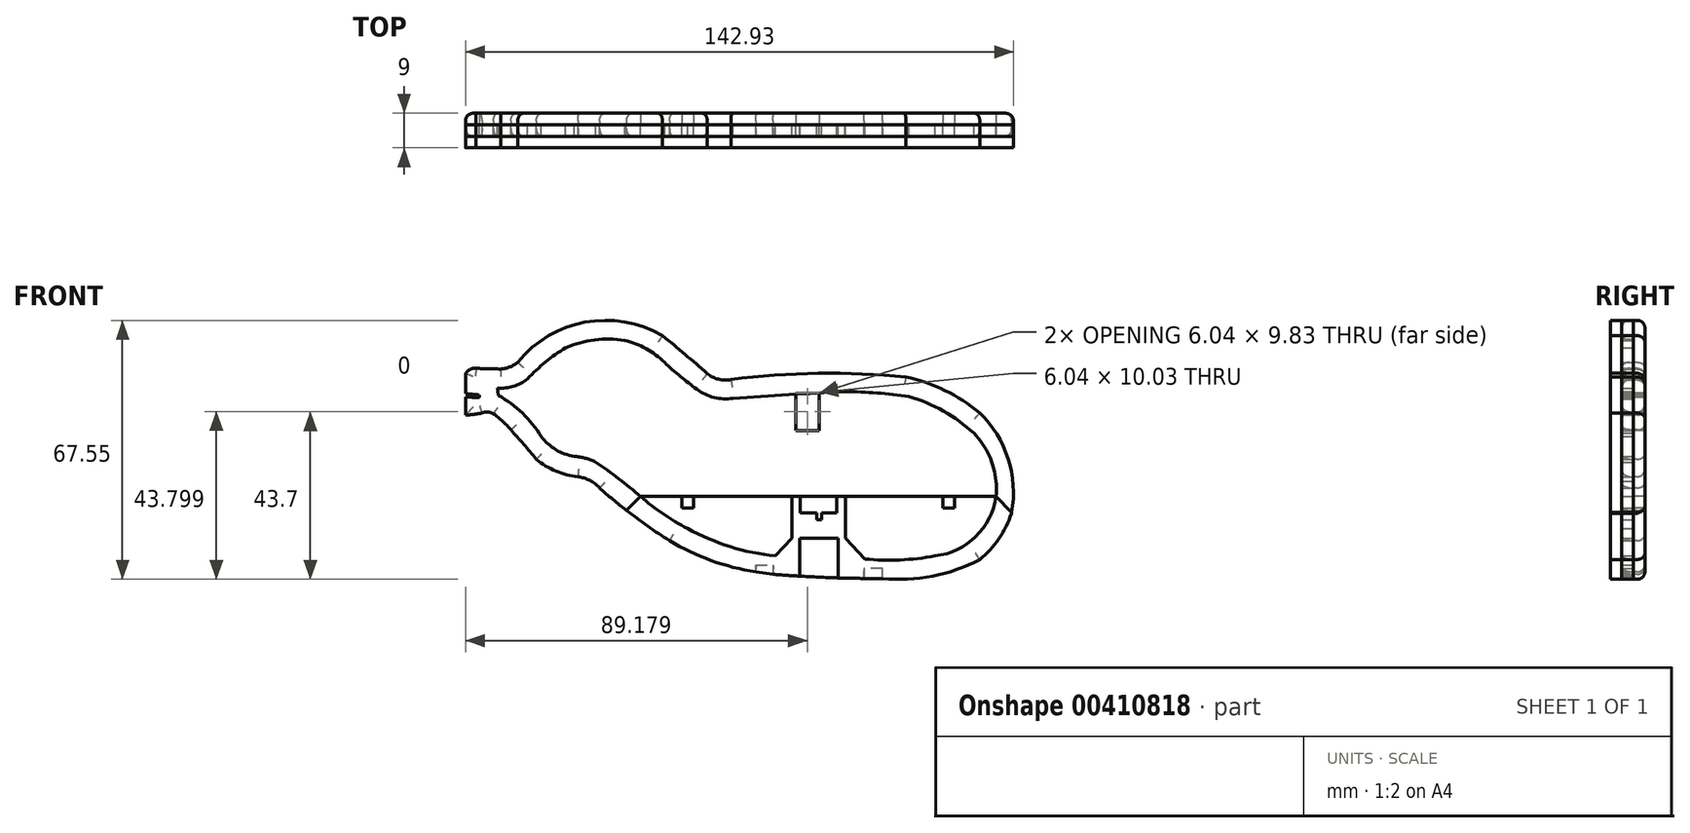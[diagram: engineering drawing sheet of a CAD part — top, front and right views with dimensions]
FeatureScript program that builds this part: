
annotation { "Feature Type Name" : "Feature", "Feature Type Description" : "" }
export const myFeature = defineFeature(function(context is Context, id is Id, definition is map)
    precondition{}
    {
        {
            var Q0;
            Q0=qCreatedBy(makeId("Front.planeOp"),FACE);
            var sketch = newSketch(context, id + "F0", { "sketchPlane" : qUnion([Q0])});
            skArc(sketch, "E0", {"start": v(-22.58, 34.57) * mm, "mid": v(-42.73, 38.11) * mm, "end": v(-60.32, 27.66) * mm});
            skArc(sketch, "E1", {"start": v(-10.89, 24.63) * mm, "mid": v(-16.66, 29.68) * mm, "end": v(-22.58, 34.57) * mm});
            skArc(sketch, "E2", {"start": v(-10.89, 24.63) * mm, "mid": v(-7.95, 23.24) * mm, "end": v(-4.7, 23.15) * mm});
            skArc(sketch, "E3", {"start": v(40.9, 23.83) * mm, "mid": v(18.08, 24.76) * mm, "end": v(-4.7, 23.15) * mm});
            skArc(sketch, "E4", {"start": v(60.17, 14.42) * mm, "mid": v(51.11, 20.3) * mm, "end": v(40.9, 23.83) * mm});
            skArc(sketch, "E5", {"start": v(68.44, -11.76) * mm, "mid": v(67.63, 2.38) * mm, "end": v(60.17, 14.42) * mm});
            skArc(sketch, "E6", {"start": v(60.17, -23.8) * mm, "mid": v(65.16, -18.37) * mm, "end": v(68.44, -11.76) * mm});
            skArc(sketch, "E7", {"start": v(34.76, -28.73) * mm, "mid": v(47.83, -28.14) * mm, "end": v(60.17, -23.8) * mm});
            skArc(sketch, "E8", {"start": v(-20.75, -18.88) * mm, "mid": v(-9.89, -24.03) * mm, "end": v(1.76, -27.02) * mm});
            skArc(sketch, "E9", {"start": v(-39, -5.12) * mm, "mid": v(-30.15, -12.37) * mm, "end": v(-20.75, -18.88) * mm});
            skArc(sketch, "E10", {"start": v(-39, -5.12) * mm, "mid": v(-41.52, -3.16) * mm, "end": v(-44.58, -2.2) * mm});
            skArc(sketch, "E11", {"start": v(-55.48, 2.36) * mm, "mid": v(-50.37, -0.73) * mm, "end": v(-44.58, -2.2) * mm});
            skArc(sketch, "E12", {"start": v(-55.48, 2.36) * mm, "mid": v(-58.75, 6.24) * mm, "end": v(-62.14, 10.03) * mm});
            skArc(sketch, "E13", {"start": v(-62.14, 10.03) * mm, "mid": v(-64.26, 12.25) * mm, "end": v(-66.65, 14.2) * mm});
            skArc(sketch, "E14", {"start": v(-66.65, 14.2) * mm, "mid": v(-68.1, 14.69) * mm, "end": v(-69.6, 14.44) * mm});
            skArc(sketch, "E15", {"start": v(-73.93, 13.86) * mm, "mid": v(-71.75, 14.07) * mm, "end": v(-69.6, 14.44) * mm});
            skArc(sketch, "E16", {"start": v(-73.93, 18.66) * mm, "mid": v(-73.95, 16.26) * mm, "end": v(-73.93, 13.86) * mm});
            skArc(sketch, "E17", {"start": v(-73.93, 18.66) * mm, "mid": v(-72.16, 18.52) * mm, "end": v(-70.38, 18.41) * mm});
            skArc(sketch, "E18", {"start": v(-70.38, 18.41) * mm, "mid": v(-70.33, 18.77) * mm, "end": v(-70.38, 19.13) * mm});
            skArc(sketch, "E19", {"start": v(-70.38, 19.13) * mm, "mid": v(-72.15, 19.31) * mm, "end": v(-73.93, 19.46) * mm});
            skArc(sketch, "E20", {"start": v(-73.93, 24.73) * mm, "mid": v(-73.96, 22.1) * mm, "end": v(-73.93, 19.46) * mm});
            skArc(sketch, "E21", {"start": v(-71.2, 26.08) * mm, "mid": v(-72.76, 25.8) * mm, "end": v(-73.93, 24.73) * mm});
            skArc(sketch, "E22", {"start": v(-71.2, 26.08) * mm, "mid": v(-68, 25.93) * mm, "end": v(-64.8, 25.9) * mm});
            skArc(sketch, "E23", {"start": v(-64.8, 25.9) * mm, "mid": v(-62.41, 26.4) * mm, "end": v(-60.32, 27.66) * mm});
            skLineSegment(sketch, "E24", {"start": v(1.76, -27.02) * mm, "end": v(1.76, -25.28) * mm});
            skLineSegment(sketch, "E25", {"start": v(1.76, -25.28) * mm, "end": v(6.25, -25.28) * mm});
            skLineSegment(sketch, "E26", {"start": v(6.25, -25.28) * mm, "end": v(6.25, -27.65) * mm});
            skLineSegment(sketch, "E27", {"start": v(34.76, -28.73) * mm, "end": v(34.76, -26.12) * mm});
            skLineSegment(sketch, "E28", {"start": v(34.76, -26.12) * mm, "end": v(30.01, -26.12) * mm});
            skLineSegment(sketch, "E29", {"start": v(30.01, -26.12) * mm, "end": v(30.01, -28.73) * mm});
            skArc(sketch, "E30", {"start": v(6.25, -27.65) * mm, "mid": v(18.13, -28.4) * mm, "end": v(30.01, -28.73) * mm});
            skLineSegment(sketch, "E31", {"start": v(-31.93, -11) * mm, "end": v(-28.25, -7.37) * mm});
            skLineSegment(sketch, "E32", {"start": v(68.52, -11.52) * mm, "end": v(64.41, -7.34) * mm});
            skLineSegment(sketch, "E33", {"start": v(-28.25, -7.37) * mm, "end": v(64.41, -7.34) * mm});
            skArc(sketch, "E34", {"start": v(-65.6, 20.9) * mm, "mid": v(-61.47, 21.4) * mm, "end": v(-57.78, 23.3) * mm});
            skArc(sketch, "E35", {"start": v(-47.8, 31.46) * mm, "mid": v(-53.07, 27.71) * mm, "end": v(-57.78, 23.3) * mm});
            skArc(sketch, "E36", {"start": v(-32.42, 33.36) * mm, "mid": v(-40.25, 33.5) * mm, "end": v(-47.8, 31.46) * mm});
            skArc(sketch, "E37", {"start": v(-22.02, 27.61) * mm, "mid": v(-26.83, 31.2) * mm, "end": v(-32.42, 33.36) * mm});
            skArc(sketch, "E38", {"start": v(-22.02, 27.61) * mm, "mid": v(-17.93, 23.98) * mm, "end": v(-13.61, 20.6) * mm});
            skArc(sketch, "E39", {"start": v(-13.61, 20.6) * mm, "mid": v(-9.14, 18.48) * mm, "end": v(-4.19, 18.23) * mm});
            skArc(sketch, "E40", {"start": v(25, 19.97) * mm, "mid": v(10.4, 19.22) * mm, "end": v(-4.19, 18.23) * mm});
            skArc(sketch, "E41", {"start": v(41.7, 18.7) * mm, "mid": v(33.37, 19.66) * mm, "end": v(25, 19.97) * mm});
            skArc(sketch, "E42", {"start": v(58.64, 9.15) * mm, "mid": v(50.71, 14.9) * mm, "end": v(41.7, 18.7) * mm});
            skArc(sketch, "E43", {"start": v(64.41, -3.4) * mm, "mid": v(62.63, 3.38) * mm, "end": v(58.64, 9.15) * mm});
            skArc(sketch, "E44", {"start": v(64.41, -7.34) * mm, "mid": v(64.58, -5.38) * mm, "end": v(64.41, -3.4) * mm});
            skArc(sketch, "E45", {"start": v(48.53, -22.85) * mm, "mid": v(59.13, -17.82) * mm, "end": v(64.41, -7.34) * mm});
            skArc(sketch, "E46", {"start": v(30.22, -23.66) * mm, "mid": v(39.4, -23.89) * mm, "end": v(48.53, -22.85) * mm});
            skArc(sketch, "E47", {"start": v(-16, -15.7) * mm, "mid": v(-4.93, -20.45) * mm, "end": v(6.88, -22.85) * mm});
            skArc(sketch, "E48", {"start": v(-28.25, -7.37) * mm, "mid": v(-22.4, -11.93) * mm, "end": v(-16, -15.7) * mm});
            skArc(sketch, "E49", {"start": v(-28.25, -7.37) * mm, "mid": v(-33.99, -2.7) * mm, "end": v(-40, 1.63) * mm});
            skArc(sketch, "E50", {"start": v(-40, 1.63) * mm, "mid": v(-42.75, 2.66) * mm, "end": v(-45.64, 3.14) * mm});
            skArc(sketch, "E51", {"start": v(-54.18, 8.27) * mm, "mid": v(-50.42, 4.86) * mm, "end": v(-45.64, 3.14) * mm});
            skArc(sketch, "E52", {"start": v(-54.18, 8.27) * mm, "mid": v(-59.1, 14.36) * mm, "end": v(-65.38, 19.04) * mm});
            skArc(sketch, "E53", {"start": v(-65.6, 20.9) * mm, "mid": v(-65.5, 19.96) * mm, "end": v(-65.38, 19.04) * mm});
            skLineSegment(sketch, "E54", {"start": v(13.17, -28.13) * mm, "end": v(13.17, -18.3) * mm});
            skLineSegment(sketch, "E55", {"start": v(13.17, -18.3) * mm, "end": v(23.23, -18.3) * mm});
            skLineSegment(sketch, "E56", {"start": v(23.23, -18.3) * mm, "end": v(23.23, -28.59) * mm});
            skLineSegment(sketch, "E57", {"start": v(6.88, -22.85) * mm, "end": v(11.22, -18.3) * mm});
            skLineSegment(sketch, "E58", {"start": v(11.22, -18.3) * mm, "end": v(11.22, -7.36) * mm});
            skLineSegment(sketch, "E59", {"start": v(13.33, -7.36) * mm, "end": v(13.33, -11.63) * mm});
            skLineSegment(sketch, "E60", {"start": v(13.33, -11.63) * mm, "end": v(17.72, -11.63) * mm});
            skLineSegment(sketch, "E61", {"start": v(17.72, -11.63) * mm, "end": v(17.72, -13.39) * mm});
            skLineSegment(sketch, "E62", {"start": v(17.72, -13.39) * mm, "end": v(18.88, -13.39) * mm});
            skLineSegment(sketch, "E63", {"start": v(18.88, -13.39) * mm, "end": v(18.88, -11.63) * mm});
            skLineSegment(sketch, "E64", {"start": v(18.88, -11.63) * mm, "end": v(22.87, -11.63) * mm});
            skLineSegment(sketch, "E65", {"start": v(22.87, -11.63) * mm, "end": v(22.86, -7.35) * mm});
            skLineSegment(sketch, "E66", {"start": v(25.1, -7.35) * mm, "end": v(25.1, -18.3) * mm});
            skLineSegment(sketch, "E67", {"start": v(25.1, -18.3) * mm, "end": v(30.22, -23.66) * mm});
            skLineSegment(sketch, "E68", {"start": v(-17.45, -7.36) * mm, "end": v(-17.45, -10.4) * mm});
            skLineSegment(sketch, "E69", {"start": v(-17.45, -10.4) * mm, "end": v(-14.45, -10.4) * mm});
            skLineSegment(sketch, "E70", {"start": v(-14.45, -10.4) * mm, "end": v(-14.45, -7.36) * mm});
            skLineSegment(sketch, "E71", {"start": v(50.57, -7.35) * mm, "end": v(50.57, -10.4) * mm});
            skLineSegment(sketch, "E72", {"start": v(50.57, -10.4) * mm, "end": v(53.57, -10.4) * mm});
            skLineSegment(sketch, "E73", {"start": v(53.57, -10.4) * mm, "end": v(53.57, -7.35) * mm});
            skLineSegment(sketch, "E74.bottom", {"start": v(12.2, 19.85) * mm, "end": v(18.24, 19.85) * mm});
            skLineSegment(sketch, "E74.top", {"start": v(12.2, 9.82) * mm, "end": v(18.24, 9.82) * mm});
            skLineSegment(sketch, "E74.left", {"start": v(12.2, 19.85) * mm, "end": v(12.2, 9.82) * mm});
            skLineSegment(sketch, "E74.right", {"start": v(18.24, 19.85) * mm, "end": v(18.24, 9.82) * mm});
            skLineSegment(sketch, "E75", {"start": v(1.76, -27.02) * mm, "end": v(6.25, -27.65) * mm});
            skLineSegment(sketch, "E76", {"start": v(30.01, -28.73) * mm, "end": v(34.76, -28.73) * mm});
            skLineSegment(sketch, "E77.bottom", {"start": v(11.2, -7.36) * mm, "end": v(-3.8, -7.36) * mm});
            skLineSegment(sketch, "E77.top", {"start": v(8.2, 6.4) * mm, "end": v(-0.8, 6.4) * mm});
            skLineSegment(sketch, "E77.left", {"start": v(11.2, -7.36) * mm, "end": v(11.2, 3.4) * mm});
            skLineSegment(sketch, "E77.right", {"start": v(-3.8, -7.36) * mm, "end": v(-3.8, 3.4) * mm});
            skLineSegment(sketch, "E78.bottom", {"start": v(28.16, 6.4) * mm, "end": v(37.16, 6.4) * mm});
            skLineSegment(sketch, "E78.top", {"start": v(25.16, -7.35) * mm, "end": v(40.16, -7.35) * mm});
            skLineSegment(sketch, "E78.left", {"start": v(25.16, 3.4) * mm, "end": v(25.16, -7.35) * mm});
            skLineSegment(sketch, "E78.right", {"start": v(40.16, 3.4) * mm, "end": v(40.16, -7.35) * mm});
            skLineSegment(sketch, "E79", {"start": v(-35.06, -1.89) * mm, "end": v(64.23, -1.89) * mm});
            skPoint(sketch, "E80.visualSharp", {"position": v(11.2, 6.4) * mm});
            skArc(sketch, "E80.filletArc", {"start": v(11.2, 3.4) * mm, "mid": v(10.32, 5.52) * mm, "end": v(8.2, 6.4) * mm});
            skPoint(sketch, "E81.visualSharp", {"position": v(-3.8, 6.4) * mm});
            skArc(sketch, "E81.filletArc", {"start": v(-0.8, 6.4) * mm, "mid": v(-2.92, 5.52) * mm, "end": v(-3.8, 3.4) * mm});
            skPoint(sketch, "E82.visualSharp", {"position": v(25.16, 6.4) * mm});
            skArc(sketch, "E82.filletArc", {"start": v(28.16, 6.4) * mm, "mid": v(26.04, 5.52) * mm, "end": v(25.16, 3.4) * mm});
            skPoint(sketch, "E83.visualSharp", {"position": v(40.16, 6.4) * mm});
            skArc(sketch, "E83.filletArc", {"start": v(40.16, 3.4) * mm, "mid": v(39.28, 5.52) * mm, "end": v(37.16, 6.4) * mm});
            skSolve(sketch);
        }
        {
            var Q0;
            Q0 = qSketchRegion(id + "F0", true);
            var Q1;
            Q1=makeQuery(id+"F0.imprint","IMPRINT",FACE,{"disambiguationData":[TD([[makeQuery(id+"F0.imprint","IMPRINT",EDGE,{"derivedFrom":sQuery(id+"F0.wireOp",EDGE,"E34")}),-1.0]])]});
            var Q2;
            Q2=makeQuery(id+"F0.imprint","IMPRINT",FACE,{"disambiguationData":[TD([[makeQuery(id+"F0.imprint","IMPRINT",EDGE,{"derivedFrom":sQuery(id+"F0.wireOp",EDGE,"E47")}),1.0]])]});
            var Q3;
            {var subQ0=sQuery(id+"F0.wireOp",EDGE,"E45");Q3=makeQuery(id+"F0.imprint","IMPRINT",FACE,{"disambiguationData":[TD([[makeQuery(id+"F0.imprint","IMPRINT",EDGE,{"derivedFrom":subQ0}),1.0]])]});}
            var Q4;
            Q4=makeQuery(id+"F0.imprint","IMPRINT",FACE,{"disambiguationData":[TD([[makeQuery(id+"F0.imprint","IMPRINT",EDGE,{"derivedFrom":sQuery(id+"F0.wireOp",EDGE,"E78.bottom")}),-1.0]])]});
            var Q5;
            Q5=makeQuery(id+"F0.imprint","IMPRINT",FACE,{"disambiguationData":[TD([[makeQuery(id+"F0.imprint","IMPRINT",EDGE,{"derivedFrom":sQuery(id+"F0.wireOp",EDGE,"E77.top")}),1.0]])]});
            var Q6;
            {var subQ0=sQuery(id+"F0.wireOp",EDGE,"E59");Q6=makeQuery(id+"F0.imprint","IMPRINT",FACE,{"disambiguationData":[TD([[makeQuery(id+"F0.imprint","IMPRINT",EDGE,{"derivedFrom":subQ0}),1.0]])]});}
            var Q7;
            {var subQ4=sQuery(id+"F0.wireOp",EDGE,"E78.top");Q7=makeQuery(id+"F0.imprint","IMPRINT",FACE,{"disambiguationData":[TD([[makeQuery(id+"F0.imprint","IMPRINT",EDGE,{"derivedFrom":subQ4}),-1.0]])]});}
            var Q8;
            {var subQ0=sQuery(id+"F0.wireOp",EDGE,"E78.top");Q8=makeQuery(id+"F0.imprint","IMPRINT",FACE,{"disambiguationData":[TD([[makeQuery(id+"F0.imprint","IMPRINT",EDGE,{"derivedFrom":subQ0}),1.0]])]});}
            var Q9;
            {var subQ0=sQuery(id+"F0.wireOp",EDGE,"E44");Q9=makeQuery(id+"F0.imprint","IMPRINT",FACE,{"disambiguationData":[TD([[makeQuery(id+"F0.imprint","IMPRINT",EDGE,{"derivedFrom":subQ0}),1.0]])]});}
            var Q10;
            {var subQ0=sQuery(id+"F0.wireOp",EDGE,"E77.bottom");Q10=makeQuery(id+"F0.imprint","IMPRINT",FACE,{"disambiguationData":[TD([[makeQuery(id+"F0.imprint","IMPRINT",EDGE,{"derivedFrom":subQ0}),-1.0]])]});}
            var Q11;
            {var subQ6=sQuery(id+"F0.wireOp",EDGE,"E77.bottom");Q11=makeQuery(id+"F0.imprint","IMPRINT",FACE,{"disambiguationData":[TD([[makeQuery(id+"F0.imprint","IMPRINT",EDGE,{"derivedFrom":subQ6}),1.0]])]});}
            var Q12;
            {var subQ5=sQuery(id+"F0.wireOp",EDGE,"E74.top");Q12=makeQuery(id+"F0.imprint","IMPRINT",FACE,{"disambiguationData":[TD([[makeQuery(id+"F0.imprint","IMPRINT",EDGE,{"derivedFrom":subQ5}),1.0]])]});}
            var Q13;
            {var subQ0=sQuery(id+"F0.wireOp",EDGE,"E71");Q13=makeQuery(id+"F0.imprint","IMPRINT",FACE,{"disambiguationData":[TD([[makeQuery(id+"F0.imprint","IMPRINT",EDGE,{"derivedFrom":subQ0}),1.0]])]});}
            var Q14;
            {var subQ0=sQuery(id+"F0.wireOp",EDGE,"E68");Q14=makeQuery(id+"F0.imprint","IMPRINT",FACE,{"disambiguationData":[TD([[makeQuery(id+"F0.imprint","IMPRINT",EDGE,{"derivedFrom":subQ0}),1.0]])]});}
            var Q15;
            {var subQ5=sQuery(id+"F0.wireOp",EDGE,"E74.bottom");Q15=makeQuery(id+"F0.imprint","IMPRINT",FACE,{"disambiguationData":[TD([[makeQuery(id+"F0.imprint","IMPRINT",EDGE,{"derivedFrom":subQ5}),-1.0]])]});}
            extrude(context, id + "F1", {"entities" : qUnion([Q0, Q1, Q2, Q3, Q4, Q5, Q6, Q7, Q8, Q9, Q10, Q11, Q12, Q13, Q14, Q15]), "depth" : 3 * mm, "offsetDistance" : 25 * mm});
        }
        {
            var Q0;
            Q0=makeQuery(id+"F0.imprint","IMPRINT",FACE,{"disambiguationData":[TD([[makeQuery(id+"F0.imprint","IMPRINT",EDGE,{"derivedFrom":sQuery(id+"F0.wireOp",EDGE,"E0")}),1.0]])]});
            extrude(context, id + "F2", {"entities" : qUnion([Q0]), "depth" : 3 * mm, "offsetDistance" : 25 * mm});
        }
        {
            var Q0;
            Q0=makeQuery(id+"F0.imprint","IMPRINT",FACE,{"disambiguationData":[TD([[makeQuery(id+"F0.imprint","IMPRINT",EDGE,{"derivedFrom":sQuery(id+"F0.wireOp",EDGE,"E34")}),-1.0]])]});
            var Q1;
            Q1=makeQuery(id+"F0.imprint","IMPRINT",FACE,{"disambiguationData":[TD([[makeQuery(id+"F0.imprint","IMPRINT",EDGE,{"derivedFrom":sQuery(id+"F0.wireOp",EDGE,"E77.top")}),1.0]])]});
            var Q2;
            Q2=makeQuery(id+"F0.imprint","IMPRINT",FACE,{"disambiguationData":[TD([[makeQuery(id+"F0.imprint","IMPRINT",EDGE,{"derivedFrom":sQuery(id+"F0.wireOp",EDGE,"E78.bottom")}),-1.0]])]});
            var Q3;
            Q3=makeQuery(id+"F0.imprint","IMPRINT",FACE,{"disambiguationData":[TD([[makeQuery(id+"F0.imprint","IMPRINT",EDGE,{"derivedFrom":sQuery(id+"F0.wireOp",EDGE,"E0")}),1.0]])]});
            var Q4;
            {var subQ6=sQuery(id+"F0.wireOp",EDGE,"E77.bottom");Q4=makeQuery(id+"F0.imprint","IMPRINT",FACE,{"disambiguationData":[TD([[makeQuery(id+"F0.imprint","IMPRINT",EDGE,{"derivedFrom":subQ6}),1.0]])]});}
            var Q5;
            {var subQ0=sQuery(id+"F0.wireOp",EDGE,"E77.bottom");Q5=makeQuery(id+"F0.imprint","IMPRINT",FACE,{"disambiguationData":[TD([[makeQuery(id+"F0.imprint","IMPRINT",EDGE,{"derivedFrom":subQ0}),-1.0]])]});}
            var Q6;
            {var subQ0=sQuery(id+"F0.wireOp",EDGE,"E44");Q6=makeQuery(id+"F0.imprint","IMPRINT",FACE,{"disambiguationData":[TD([[makeQuery(id+"F0.imprint","IMPRINT",EDGE,{"derivedFrom":subQ0}),1.0]])]});}
            var Q7;
            {var subQ0=sQuery(id+"F0.wireOp",EDGE,"E78.top");Q7=makeQuery(id+"F0.imprint","IMPRINT",FACE,{"disambiguationData":[TD([[makeQuery(id+"F0.imprint","IMPRINT",EDGE,{"derivedFrom":subQ0}),1.0]])]});}
            var Q8;
            {var subQ4=sQuery(id+"F0.wireOp",EDGE,"E78.top");Q8=makeQuery(id+"F0.imprint","IMPRINT",FACE,{"disambiguationData":[TD([[makeQuery(id+"F0.imprint","IMPRINT",EDGE,{"derivedFrom":subQ4}),-1.0]])]});}
            extrude(context, id + "F3", {"entities" : qUnion([Q0, Q1, Q2, Q3, Q4, Q5, Q6, Q7, Q8]), "depth" : 3 * mm, "offsetDistance" : 25 * mm});
        }
        {
            var Q0;
            Q0=makeQuery(id+"F1.opExtrude","SWEPT_BODY",BODY,{"disambiguationData":[OSD([sQuery(id+"F0.wireOp",EDGE,"E0"),sQuery(id+"F0.wireOp",EDGE,"E1"),sQuery(id+"F0.wireOp",EDGE,"E2"),sQuery(id+"F0.wireOp",EDGE,"E3"),sQuery(id+"F0.wireOp",EDGE,"E4"),sQuery(id+"F0.wireOp",EDGE,"E5"),sQuery(id+"F0.wireOp",EDGE,"E6"),sQuery(id+"F0.wireOp",EDGE,"E7"),sQuery(id+"F0.wireOp",EDGE,"E8"),sQuery(id+"F0.wireOp",EDGE,"E9"),sQuery(id+"F0.wireOp",EDGE,"E10"),sQuery(id+"F0.wireOp",EDGE,"E11"),sQuery(id+"F0.wireOp",EDGE,"E12"),sQuery(id+"F0.wireOp",EDGE,"E13"),sQuery(id+"F0.wireOp",EDGE,"E14"),sQuery(id+"F0.wireOp",EDGE,"E15"),sQuery(id+"F0.wireOp",EDGE,"E16"),sQuery(id+"F0.wireOp",EDGE,"E17"),sQuery(id+"F0.wireOp",EDGE,"E18"),sQuery(id+"F0.wireOp",EDGE,"E19"),sQuery(id+"F0.wireOp",EDGE,"E20"),sQuery(id+"F0.wireOp",EDGE,"E21"),sQuery(id+"F0.wireOp",EDGE,"E22"),sQuery(id+"F0.wireOp",EDGE,"E23"),sQuery(id+"F0.wireOp",EDGE,"E30"),sQuery(id+"F0.wireOp",EDGE,"E75"),sQuery(id+"F0.wireOp",EDGE,"E76")])]});
            deleteBodies(context, id + "F4", {"entities" : qUnion([Q0])});
        }
        {
            var Q0;
            Q0=makeQuery(id+"F0.imprint","IMPRINT",FACE,{"disambiguationData":[TD([[makeQuery(id+"F0.imprint","IMPRINT",EDGE,{"derivedFrom":sQuery(id+"F0.wireOp",EDGE,"E0")}),1.0]])]});
            var Q1;
            Q1=makeQuery(id+"F0.imprint","IMPRINT",FACE,{"disambiguationData":[TD([[makeQuery(id+"F0.imprint","IMPRINT",EDGE,{"derivedFrom":sQuery(id+"F0.wireOp",EDGE,"E34")}),-1.0]])]});
            var Q2;
            Q2=makeQuery(id+"F0.imprint","IMPRINT",FACE,{"disambiguationData":[TD([[makeQuery(id+"F0.imprint","IMPRINT",EDGE,{"derivedFrom":sQuery(id+"F0.wireOp",EDGE,"E77.top")}),1.0]])]});
            var Q3;
            {var subQ0=sQuery(id+"F0.wireOp",EDGE,"E77.bottom");Q3=makeQuery(id+"F0.imprint","IMPRINT",FACE,{"disambiguationData":[TD([[makeQuery(id+"F0.imprint","IMPRINT",EDGE,{"derivedFrom":subQ0}),-1.0]])]});}
            var Q4;
            {var subQ4=sQuery(id+"F0.wireOp",EDGE,"E78.top");Q4=makeQuery(id+"F0.imprint","IMPRINT",FACE,{"disambiguationData":[TD([[makeQuery(id+"F0.imprint","IMPRINT",EDGE,{"derivedFrom":subQ4}),-1.0]])]});}
            var Q5;
            {var subQ0=sQuery(id+"F0.wireOp",EDGE,"E78.top");Q5=makeQuery(id+"F0.imprint","IMPRINT",FACE,{"disambiguationData":[TD([[makeQuery(id+"F0.imprint","IMPRINT",EDGE,{"derivedFrom":subQ0}),1.0]])]});}
            var Q6;
            Q6=makeQuery(id+"F0.imprint","IMPRINT",FACE,{"disambiguationData":[TD([[makeQuery(id+"F0.imprint","IMPRINT",EDGE,{"derivedFrom":sQuery(id+"F0.wireOp",EDGE,"E78.bottom")}),-1.0]])]});
            var Q7;
            {var subQ0=sQuery(id+"F0.wireOp",EDGE,"E44");Q7=makeQuery(id+"F0.imprint","IMPRINT",FACE,{"disambiguationData":[TD([[makeQuery(id+"F0.imprint","IMPRINT",EDGE,{"derivedFrom":subQ0}),1.0]])]});}
            var Q8;
            {var subQ6=sQuery(id+"F0.wireOp",EDGE,"E77.bottom");Q8=makeQuery(id+"F0.imprint","IMPRINT",FACE,{"disambiguationData":[TD([[makeQuery(id+"F0.imprint","IMPRINT",EDGE,{"derivedFrom":subQ6}),1.0]])]});}
            var Q9;
            {var subQ5=sQuery(id+"F0.wireOp",EDGE,"E74.bottom");Q9=makeQuery(id+"F0.imprint","IMPRINT",FACE,{"disambiguationData":[TD([[makeQuery(id+"F0.imprint","IMPRINT",EDGE,{"derivedFrom":subQ5}),-1.0]])]});}
            extrude(context, id + "F5", {"entities" : qUnion([Q0, Q1, Q2, Q3, Q4, Q5, Q6, Q7, Q8, Q9]), "depth" : 3 * mm, "offsetDistance" : 25 * mm});
        }
        {
            var Q0;
            Q0=makeQuery(id+"F0.imprint","IMPRINT",FACE,{"disambiguationData":[TD([[makeQuery(id+"F0.imprint","IMPRINT",EDGE,{"derivedFrom":sQuery(id+"F0.wireOp",EDGE,"E0")}),1.0]])]});
            var Q1;
            {var subQ5=sQuery(id+"F0.wireOp",EDGE,"E74.bottom");Q1=makeQuery(id+"F0.imprint","IMPRINT",FACE,{"disambiguationData":[TD([[makeQuery(id+"F0.imprint","IMPRINT",EDGE,{"derivedFrom":subQ5}),-1.0]])]});}
            extrude(context, id + "F6", {"entities" : qUnion([Q0, Q1]), "depth" : 6 * mm, "offsetDistance" : 25 * mm});
        }
        {
            var Q0;
            Q0=makeQuery(id+"F0.imprint","IMPRINT",FACE,{"disambiguationData":[TD([[makeQuery(id+"F0.imprint","IMPRINT",EDGE,{"derivedFrom":sQuery(id+"F0.wireOp",EDGE,"E0")}),1.0]])]});
            var Q1;
            Q1=makeQuery(id+"F0.imprint","IMPRINT",FACE,{"disambiguationData":[TD([[makeQuery(id+"F0.imprint","IMPRINT",EDGE,{"derivedFrom":sQuery(id+"F0.wireOp",EDGE,"E34")}),-1.0]])]});
            var Q2;
            {var subQ0=sQuery(id+"F0.wireOp",EDGE,"E77.bottom");Q2=makeQuery(id+"F0.imprint","IMPRINT",FACE,{"disambiguationData":[TD([[makeQuery(id+"F0.imprint","IMPRINT",EDGE,{"derivedFrom":subQ0}),-1.0]])]});}
            var Q3;
            {var subQ0=sQuery(id+"F0.wireOp",EDGE,"E78.top");Q3=makeQuery(id+"F0.imprint","IMPRINT",FACE,{"disambiguationData":[TD([[makeQuery(id+"F0.imprint","IMPRINT",EDGE,{"derivedFrom":subQ0}),1.0]])]});}
            var Q4;
            Q4=makeQuery(id+"F0.imprint","IMPRINT",FACE,{"disambiguationData":[TD([[makeQuery(id+"F0.imprint","IMPRINT",EDGE,{"derivedFrom":sQuery(id+"F0.wireOp",EDGE,"E78.bottom")}),-1.0]])]});
            var Q5;
            {var subQ0=sQuery(id+"F0.wireOp",EDGE,"E44");Q5=makeQuery(id+"F0.imprint","IMPRINT",FACE,{"disambiguationData":[TD([[makeQuery(id+"F0.imprint","IMPRINT",EDGE,{"derivedFrom":subQ0}),1.0]])]});}
            var Q6;
            {var subQ4=sQuery(id+"F0.wireOp",EDGE,"E78.top");Q6=makeQuery(id+"F0.imprint","IMPRINT",FACE,{"disambiguationData":[TD([[makeQuery(id+"F0.imprint","IMPRINT",EDGE,{"derivedFrom":subQ4}),-1.0]])]});}
            var Q7;
            {var subQ6=sQuery(id+"F0.wireOp",EDGE,"E77.bottom");Q7=makeQuery(id+"F0.imprint","IMPRINT",FACE,{"disambiguationData":[TD([[makeQuery(id+"F0.imprint","IMPRINT",EDGE,{"derivedFrom":subQ6}),1.0]])]});}
            var Q8;
            Q8=makeQuery(id+"F0.imprint","IMPRINT",FACE,{"disambiguationData":[TD([[makeQuery(id+"F0.imprint","IMPRINT",EDGE,{"derivedFrom":sQuery(id+"F0.wireOp",EDGE,"E77.top")}),1.0]])]});
            var Q9;
            {var subQ5=sQuery(id+"F0.wireOp",EDGE,"E74.bottom");Q9=makeQuery(id+"F0.imprint","IMPRINT",FACE,{"disambiguationData":[TD([[makeQuery(id+"F0.imprint","IMPRINT",EDGE,{"derivedFrom":subQ5}),-1.0]])]});}
            extrude(context, id + "F7", {"entities" : qUnion([Q0, Q1, Q2, Q3, Q4, Q5, Q6, Q7, Q8, Q9]), "depth" : -3 * mm, "offsetDistance" : 25 * mm});
        }
        {
            var Q0;
            Q0=makeQuery(id+"F7.opExtrude","CAP_EDGE",EDGE,{"disambiguationData":[OSD([sQuery(id+"F0.wireOp",EDGE,"E5")])],"isStart":false});
            var Q1;
            Q1=makeQuery(id+"F7.opExtrude","CAP_EDGE",EDGE,{"disambiguationData":[OSD([sQuery(id+"F0.wireOp",EDGE,"E4")])],"isStart":false});
            var Q2;
            Q2=makeQuery(id+"F7.opExtrude","CAP_EDGE",EDGE,{"disambiguationData":[OSD([sQuery(id+"F0.wireOp",EDGE,"E3")])],"isStart":false});
            var Q3;
            Q3=makeQuery(id+"F7.opExtrude","CAP_EDGE",EDGE,{"disambiguationData":[OSD([sQuery(id+"F0.wireOp",EDGE,"E2")])],"isStart":false});
            var Q4;
            Q4=makeQuery(id+"F7.opExtrude","CAP_EDGE",EDGE,{"disambiguationData":[OSD([sQuery(id+"F0.wireOp",EDGE,"E1")])],"isStart":false});
            var Q5;
            Q5=makeQuery(id+"F7.opExtrude","CAP_EDGE",EDGE,{"disambiguationData":[OSD([sQuery(id+"F0.wireOp",EDGE,"E0")])],"isStart":false});
            var Q6;
            Q6=makeQuery(id+"F7.opExtrude","CAP_EDGE",EDGE,{"disambiguationData":[OSD([sQuery(id+"F0.wireOp",EDGE,"E23")])],"isStart":false});
            var Q7;
            Q7=makeQuery(id+"F7.opExtrude","CAP_EDGE",EDGE,{"disambiguationData":[OSD([sQuery(id+"F0.wireOp",EDGE,"E22")])],"isStart":false});
            var Q8;
            Q8=makeQuery(id+"F7.opExtrude","CAP_EDGE",EDGE,{"disambiguationData":[OSD([sQuery(id+"F0.wireOp",EDGE,"E21")])],"isStart":false});
            var Q9;
            Q9=makeQuery(id+"F7.opExtrude","CAP_EDGE",EDGE,{"disambiguationData":[OSD([sQuery(id+"F0.wireOp",EDGE,"E20")])],"isStart":false});
            var Q10;
            Q10=makeQuery(id+"F7.opExtrude","CAP_EDGE",EDGE,{"disambiguationData":[OSD([sQuery(id+"F0.wireOp",EDGE,"E16")])],"isStart":false});
            var Q11;
            Q11=makeQuery(id+"F7.opExtrude","CAP_EDGE",EDGE,{"disambiguationData":[OSD([sQuery(id+"F0.wireOp",EDGE,"E15")])],"isStart":false});
            var Q12;
            Q12=makeQuery(id+"F7.opExtrude","CAP_EDGE",EDGE,{"disambiguationData":[OSD([sQuery(id+"F0.wireOp",EDGE,"E14")])],"isStart":false});
            var Q13;
            Q13=makeQuery(id+"F7.opExtrude","CAP_EDGE",EDGE,{"disambiguationData":[OSD([sQuery(id+"F0.wireOp",EDGE,"E13")])],"isStart":false});
            var Q14;
            Q14=makeQuery(id+"F7.opExtrude","CAP_EDGE",EDGE,{"disambiguationData":[OSD([sQuery(id+"F0.wireOp",EDGE,"E12")])],"isStart":false});
            var Q15;
            Q15=makeQuery(id+"F7.opExtrude","CAP_EDGE",EDGE,{"disambiguationData":[OSD([sQuery(id+"F0.wireOp",EDGE,"E11")])],"isStart":false});
            var Q16;
            Q16=makeQuery(id+"F7.opExtrude","CAP_EDGE",EDGE,{"disambiguationData":[OSD([sQuery(id+"F0.wireOp",EDGE,"E9")])],"isStart":false});
            fillet(context, id + "F8", {"entities" : qUnion([Q0, Q1, Q2, Q3, Q4, Q5, Q6, Q7, Q8, Q9, Q10, Q11, Q12, Q13, Q14, Q15, Q16]), "radius" : 2 * mm, "tangentPropagation" : true, "allowEdgeOverflow" : false});
        }
        {
            var Q0;
            Q0=makeQuery(id+"F5.opExtrude","CAP_EDGE",EDGE,{"disambiguationData":[OSD([sQuery(id+"F0.wireOp",EDGE,"E0")])],"isStart":false});
            var Q1;
            Q1=makeQuery(id+"F5.opExtrude","CAP_EDGE",EDGE,{"disambiguationData":[OSD([sQuery(id+"F0.wireOp",EDGE,"E23")])],"isStart":false});
            var Q2;
            Q2=makeQuery(id+"F5.opExtrude","CAP_EDGE",EDGE,{"disambiguationData":[OSD([sQuery(id+"F0.wireOp",EDGE,"E22")])],"isStart":false});
            var Q3;
            Q3=makeQuery(id+"F5.opExtrude","CAP_EDGE",EDGE,{"disambiguationData":[OSD([sQuery(id+"F0.wireOp",EDGE,"E20")])],"isStart":false});
            var Q4;
            Q4=makeQuery(id+"F5.opExtrude","CAP_EDGE",EDGE,{"disambiguationData":[OSD([sQuery(id+"F0.wireOp",EDGE,"E16")])],"isStart":false});
            var Q5;
            Q5=makeQuery(id+"F5.opExtrude","CAP_EDGE",EDGE,{"disambiguationData":[OSD([sQuery(id+"F0.wireOp",EDGE,"E15")])],"isStart":false});
            var Q6;
            Q6=makeQuery(id+"F5.opExtrude","CAP_EDGE",EDGE,{"disambiguationData":[OSD([sQuery(id+"F0.wireOp",EDGE,"E14")])],"isStart":false});
            var Q7;
            Q7=makeQuery(id+"F5.opExtrude","CAP_EDGE",EDGE,{"disambiguationData":[OSD([sQuery(id+"F0.wireOp",EDGE,"E13")])],"isStart":false});
            var Q8;
            Q8=makeQuery(id+"F5.opExtrude","CAP_EDGE",EDGE,{"disambiguationData":[OSD([sQuery(id+"F0.wireOp",EDGE,"E12")])],"isStart":false});
            var Q9;
            Q9=makeQuery(id+"F5.opExtrude","CAP_EDGE",EDGE,{"disambiguationData":[OSD([sQuery(id+"F0.wireOp",EDGE,"E11")])],"isStart":false});
            var Q10;
            Q10=makeQuery(id+"F5.opExtrude","CAP_EDGE",EDGE,{"disambiguationData":[OSD([sQuery(id+"F0.wireOp",EDGE,"E10")])],"isStart":false});
            var Q11;
            Q11=makeQuery(id+"F5.opExtrude","CAP_EDGE",EDGE,{"disambiguationData":[OSD([sQuery(id+"F0.wireOp",EDGE,"E9")])],"isStart":false});
            var Q12;
            Q12=makeQuery(id+"F5.opExtrude","CAP_EDGE",EDGE,{"disambiguationData":[OSD([sQuery(id+"F0.wireOp",EDGE,"E1")])],"isStart":false});
            var Q13;
            Q13=makeQuery(id+"F5.opExtrude","CAP_EDGE",EDGE,{"disambiguationData":[OSD([sQuery(id+"F0.wireOp",EDGE,"E2")])],"isStart":false});
            var Q14;
            Q14=makeQuery(id+"F5.opExtrude","CAP_EDGE",EDGE,{"disambiguationData":[OSD([sQuery(id+"F0.wireOp",EDGE,"E3")])],"isStart":false});
            var Q15;
            Q15=makeQuery(id+"F5.opExtrude","CAP_EDGE",EDGE,{"disambiguationData":[OSD([sQuery(id+"F0.wireOp",EDGE,"E4")])],"isStart":false});
            var Q16;
            Q16=makeQuery(id+"F5.opExtrude","CAP_EDGE",EDGE,{"disambiguationData":[OSD([sQuery(id+"F0.wireOp",EDGE,"E5")])],"isStart":false});
            var Q17;
            Q17=makeQuery(id+"F5.opExtrude","CAP_EDGE",EDGE,{"disambiguationData":[OSD([sQuery(id+"F0.wireOp",EDGE,"E21")])],"isStart":false});
            fillet(context, id + "F9", {"entities" : qUnion([Q0, Q1, Q2, Q3, Q4, Q5, Q6, Q7, Q8, Q9, Q10, Q11, Q12, Q13, Q14, Q15, Q16, Q17]), "radius" : 2 * mm, "tangentPropagation" : true, "allowEdgeOverflow" : false});
        }
        {
            var Q0;
            Q0=makeQuery(id+"F0.imprint","IMPRINT",FACE,{"disambiguationData":[TD([[makeQuery(id+"F0.imprint","IMPRINT",EDGE,{"derivedFrom":sQuery(id+"F0.wireOp",EDGE,"E0")}),1.0]])]});
            var Q1;
            Q1=makeQuery(id+"F0.imprint","IMPRINT",FACE,{"disambiguationData":[TD([[makeQuery(id+"F0.imprint","IMPRINT",EDGE,{"derivedFrom":sQuery(id+"F0.wireOp",EDGE,"E34")}),-1.0]])]});
            var Q2;
            Q2=makeQuery(id+"F0.imprint","IMPRINT",FACE,{"disambiguationData":[TD([[makeQuery(id+"F0.imprint","IMPRINT",EDGE,{"derivedFrom":sQuery(id+"F0.wireOp",EDGE,"E77.top")}),1.0]])]});
            var Q3;
            Q3=makeQuery(id+"F0.imprint","IMPRINT",FACE,{"disambiguationData":[TD([[makeQuery(id+"F0.imprint","IMPRINT",EDGE,{"derivedFrom":sQuery(id+"F0.wireOp",EDGE,"E78.bottom")}),-1.0]])]});
            var Q4;
            {var subQ0=sQuery(id+"F0.wireOp",EDGE,"E78.top");Q4=makeQuery(id+"F0.imprint","IMPRINT",FACE,{"disambiguationData":[TD([[makeQuery(id+"F0.imprint","IMPRINT",EDGE,{"derivedFrom":subQ0}),1.0]])]});}
            var Q5;
            {var subQ0=sQuery(id+"F0.wireOp",EDGE,"E77.bottom");Q5=makeQuery(id+"F0.imprint","IMPRINT",FACE,{"disambiguationData":[TD([[makeQuery(id+"F0.imprint","IMPRINT",EDGE,{"derivedFrom":subQ0}),-1.0]])]});}
            var Q6;
            {var subQ4=sQuery(id+"F0.wireOp",EDGE,"E78.top");Q6=makeQuery(id+"F0.imprint","IMPRINT",FACE,{"disambiguationData":[TD([[makeQuery(id+"F0.imprint","IMPRINT",EDGE,{"derivedFrom":subQ4}),-1.0]])]});}
            var Q7;
            {var subQ0=sQuery(id+"F0.wireOp",EDGE,"E44");Q7=makeQuery(id+"F0.imprint","IMPRINT",FACE,{"disambiguationData":[TD([[makeQuery(id+"F0.imprint","IMPRINT",EDGE,{"derivedFrom":subQ0}),1.0]])]});}
            var Q8;
            {var subQ6=sQuery(id+"F0.wireOp",EDGE,"E77.bottom");Q8=makeQuery(id+"F0.imprint","IMPRINT",FACE,{"disambiguationData":[TD([[makeQuery(id+"F0.imprint","IMPRINT",EDGE,{"derivedFrom":subQ6}),1.0]])]});}
            var Q9;
            {var subQ5=sQuery(id+"F0.wireOp",EDGE,"E74.top");Q9=makeQuery(id+"F0.imprint","IMPRINT",FACE,{"disambiguationData":[TD([[makeQuery(id+"F0.imprint","IMPRINT",EDGE,{"derivedFrom":subQ5}),1.0]])]});}
            var Q10;
            {var subQ5=sQuery(id+"F0.wireOp",EDGE,"E74.bottom");Q10=makeQuery(id+"F0.imprint","IMPRINT",FACE,{"disambiguationData":[TD([[makeQuery(id+"F0.imprint","IMPRINT",EDGE,{"derivedFrom":subQ5}),-1.0]])]});}
            extrude(context, id + "F10", {"entities" : qUnion([Q0, Q1, Q2, Q3, Q4, Q5, Q6, Q7, Q8, Q9, Q10]), "depth" : 3 * mm, "offsetDistance" : 25 * mm});
        }
        {
            var Q0;
            Q0=makeQuery(id+"F0.imprint","IMPRINT",FACE,{"disambiguationData":[TD([[makeQuery(id+"F0.imprint","IMPRINT",EDGE,{"derivedFrom":sQuery(id+"F0.wireOp",EDGE,"E24")}),-1.0]])]});
            var Q1;
            Q1=makeQuery(id+"F0.imprint","IMPRINT",FACE,{"disambiguationData":[TD([[makeQuery(id+"F0.imprint","IMPRINT",EDGE,{"derivedFrom":sQuery(id+"F0.wireOp",EDGE,"E27")}),1.0]])]});
            var Q2;
            {var subQ0=sQuery(id+"F0.wireOp",EDGE,"E54");Q2=makeQuery(id+"F0.imprint","IMPRINT",FACE,{"disambiguationData":[TD([[makeQuery(id+"F0.imprint","IMPRINT",EDGE,{"derivedFrom":subQ0}),-1.0]])]});}
            var Q3;
            {var subQ15=sQuery(id+"F0.wireOp",EDGE,"E6");Q3=makeQuery(id+"F0.imprint","IMPRINT",FACE,{"disambiguationData":[TD([[makeQuery(id+"F0.imprint","IMPRINT",EDGE,{"derivedFrom":subQ15}),1.0]])]});}
            var Q4;
            Q4=makeQuery(id+"F0.imprint","IMPRINT",FACE,{"disambiguationData":[TD([[makeQuery(id+"F0.imprint","IMPRINT",EDGE,{"derivedFrom":sQuery(id+"F0.wireOp",EDGE,"E47")}),1.0]])]});
            var Q5;
            {var subQ0=sQuery(id+"F0.wireOp",EDGE,"E45");Q5=makeQuery(id+"F0.imprint","IMPRINT",FACE,{"disambiguationData":[TD([[makeQuery(id+"F0.imprint","IMPRINT",EDGE,{"derivedFrom":subQ0}),1.0]])]});}
            var Q6;
            {var subQ0=sQuery(id+"F0.wireOp",EDGE,"E59");Q6=makeQuery(id+"F0.imprint","IMPRINT",FACE,{"disambiguationData":[TD([[makeQuery(id+"F0.imprint","IMPRINT",EDGE,{"derivedFrom":subQ0}),1.0]])]});}
            extrude(context, id + "F11", {"entities" : qUnion([Q0, Q1, Q2, Q3, Q4, Q5, Q6]), "depth" : 3 * mm, "offsetDistance" : 25 * mm});
        }
        {
            var Q0;
            Q0=makeQuery(id+"F0.imprint","IMPRINT",FACE,{"disambiguationData":[TD([[makeQuery(id+"F0.imprint","IMPRINT",EDGE,{"derivedFrom":sQuery(id+"F0.wireOp",EDGE,"E24")}),-1.0]])]});
            var Q1;
            Q1=makeQuery(id+"F0.imprint","IMPRINT",FACE,{"disambiguationData":[TD([[makeQuery(id+"F0.imprint","IMPRINT",EDGE,{"derivedFrom":sQuery(id+"F0.wireOp",EDGE,"E27")}),1.0]])]});
            var Q2;
            {var subQ0=sQuery(id+"F0.wireOp",EDGE,"E54");Q2=makeQuery(id+"F0.imprint","IMPRINT",FACE,{"disambiguationData":[TD([[makeQuery(id+"F0.imprint","IMPRINT",EDGE,{"derivedFrom":subQ0}),-1.0]])]});}
            var Q3;
            {var subQ15=sQuery(id+"F0.wireOp",EDGE,"E6");Q3=makeQuery(id+"F0.imprint","IMPRINT",FACE,{"disambiguationData":[TD([[makeQuery(id+"F0.imprint","IMPRINT",EDGE,{"derivedFrom":subQ15}),1.0]])]});}
            var Q4;
            Q4=makeQuery(id+"F0.imprint","IMPRINT",FACE,{"disambiguationData":[TD([[makeQuery(id+"F0.imprint","IMPRINT",EDGE,{"derivedFrom":sQuery(id+"F0.wireOp",EDGE,"E47")}),1.0]])]});
            var Q5;
            {var subQ0=sQuery(id+"F0.wireOp",EDGE,"E45");Q5=makeQuery(id+"F0.imprint","IMPRINT",FACE,{"disambiguationData":[TD([[makeQuery(id+"F0.imprint","IMPRINT",EDGE,{"derivedFrom":subQ0}),1.0]])]});}
            var Q6;
            {var subQ0=sQuery(id+"F0.wireOp",EDGE,"E59");Q6=makeQuery(id+"F0.imprint","IMPRINT",FACE,{"disambiguationData":[TD([[makeQuery(id+"F0.imprint","IMPRINT",EDGE,{"derivedFrom":subQ0}),1.0]])]});}
            extrude(context, id + "F12", {"entities" : qUnion([Q0, Q1, Q2, Q3, Q4, Q5, Q6]), "depth" : 3 * mm, "offsetDistance" : 25 * mm});
        }
        {
            var Q0;
            Q0=makeQuery(id+"F12.opExtrude","CAP_EDGE",EDGE,{"disambiguationData":[OSD([sQuery(id+"F0.wireOp",EDGE,"E9")])],"isStart":false});
            var Q1;
            Q1=makeQuery(id+"F12.opExtrude","CAP_EDGE",EDGE,{"disambiguationData":[OSD([sQuery(id+"F0.wireOp",EDGE,"E75")])],"isStart":false});
            var Q2;
            Q2=makeQuery(id+"F12.opExtrude","CAP_EDGE",EDGE,{"disambiguationData":[OSD([sQuery(id+"F0.wireOp",EDGE,"E76")])],"isStart":false});
            var Q3;
            Q3=makeQuery(id+"F12.opExtrude","CAP_EDGE",EDGE,{"disambiguationData":[OSD([sQuery(id+"F0.wireOp",EDGE,"E7")])],"isStart":false});
            var Q4;
            Q4=makeQuery(id+"F12.opExtrude","CAP_EDGE",EDGE,{"disambiguationData":[OSD([sQuery(id+"F0.wireOp",EDGE,"E6")])],"isStart":false});
            fillet(context, id + "F13", {"entities" : qUnion([Q0, Q1, Q2, Q3, Q4]), "radius" : 2 * mm, "tangentPropagation" : true, "allowEdgeOverflow" : false});
        }
        {
            var Q0;
            {var subQ15=sQuery(id+"F0.wireOp",EDGE,"E6");Q0=makeQuery(id+"F0.imprint","IMPRINT",FACE,{"disambiguationData":[TD([[makeQuery(id+"F0.imprint","IMPRINT",EDGE,{"derivedFrom":subQ15}),1.0]])]});}
            extrude(context, id + "F14", {"entities" : qUnion([Q0]), "depth" : 3 * mm, "offsetDistance" : 25 * mm});
        }
        {
            var Q0;
            Q0=makeQuery(id+"F0.imprint","IMPRINT",FACE,{"disambiguationData":[TD([[makeQuery(id+"F0.imprint","IMPRINT",EDGE,{"derivedFrom":sQuery(id+"F0.wireOp",EDGE,"E24")}),-1.0]])]});
            var Q1;
            Q1=makeQuery(id+"F0.imprint","IMPRINT",FACE,{"disambiguationData":[TD([[makeQuery(id+"F0.imprint","IMPRINT",EDGE,{"derivedFrom":sQuery(id+"F0.wireOp",EDGE,"E27")}),1.0]])]});
            var Q2;
            {var subQ15=sQuery(id+"F0.wireOp",EDGE,"E6");Q2=makeQuery(id+"F0.imprint","IMPRINT",FACE,{"disambiguationData":[TD([[makeQuery(id+"F0.imprint","IMPRINT",EDGE,{"derivedFrom":subQ15}),1.0]])]});}
            extrude(context, id + "F15", {"entities" : qUnion([Q0, Q1, Q2]), "depth" : 6 * mm, "offsetDistance" : 25 * mm});
        }
        {
            var Q0;
            Q0=makeQuery(id+"F0.imprint","IMPRINT",FACE,{"disambiguationData":[TD([[makeQuery(id+"F0.imprint","IMPRINT",EDGE,{"derivedFrom":sQuery(id+"F0.wireOp",EDGE,"E24")}),-1.0]])]});
            var Q1;
            Q1=makeQuery(id+"F0.imprint","IMPRINT",FACE,{"disambiguationData":[TD([[makeQuery(id+"F0.imprint","IMPRINT",EDGE,{"derivedFrom":sQuery(id+"F0.wireOp",EDGE,"E27")}),1.0]])]});
            var Q2;
            {var subQ0=sQuery(id+"F0.wireOp",EDGE,"E54");Q2=makeQuery(id+"F0.imprint","IMPRINT",FACE,{"disambiguationData":[TD([[makeQuery(id+"F0.imprint","IMPRINT",EDGE,{"derivedFrom":subQ0}),-1.0]])]});}
            var Q3;
            {var subQ15=sQuery(id+"F0.wireOp",EDGE,"E6");Q3=makeQuery(id+"F0.imprint","IMPRINT",FACE,{"disambiguationData":[TD([[makeQuery(id+"F0.imprint","IMPRINT",EDGE,{"derivedFrom":subQ15}),1.0]])]});}
            var Q4;
            {var subQ0=sQuery(id+"F0.wireOp",EDGE,"E45");Q4=makeQuery(id+"F0.imprint","IMPRINT",FACE,{"disambiguationData":[TD([[makeQuery(id+"F0.imprint","IMPRINT",EDGE,{"derivedFrom":subQ0}),1.0]])]});}
            var Q5;
            Q5=makeQuery(id+"F0.imprint","IMPRINT",FACE,{"disambiguationData":[TD([[makeQuery(id+"F0.imprint","IMPRINT",EDGE,{"derivedFrom":sQuery(id+"F0.wireOp",EDGE,"E47")}),1.0]])]});
            var Q6;
            {var subQ0=sQuery(id+"F0.wireOp",EDGE,"E59");Q6=makeQuery(id+"F0.imprint","IMPRINT",FACE,{"disambiguationData":[TD([[makeQuery(id+"F0.imprint","IMPRINT",EDGE,{"derivedFrom":subQ0}),1.0]])]});}
            extrude(context, id + "F16", {"entities" : qUnion([Q0, Q1, Q2, Q3, Q4, Q5, Q6]), "depth" : -3 * mm, "offsetDistance" : 25 * mm});
        }
        {
            var Q0;
            Q0=makeQuery(id+"F16.opExtrude","CAP_EDGE",EDGE,{"disambiguationData":[OSD([sQuery(id+"F0.wireOp",EDGE,"E6")])],"isStart":false});
            var Q1;
            Q1=makeQuery(id+"F16.opExtrude","CAP_EDGE",EDGE,{"disambiguationData":[OSD([sQuery(id+"F0.wireOp",EDGE,"E7")])],"isStart":false});
            var Q2;
            Q2=makeQuery(id+"F16.opExtrude","CAP_EDGE",EDGE,{"disambiguationData":[OSD([sQuery(id+"F0.wireOp",EDGE,"E76")])],"isStart":false});
            var Q3;
            Q3=makeQuery(id+"F16.opExtrude","CAP_EDGE",EDGE,{"disambiguationData":[OSD([sQuery(id+"F0.wireOp",EDGE,"E30")])],"isStart":false});
            var Q4;
            Q4=makeQuery(id+"F16.opExtrude","CAP_EDGE",EDGE,{"disambiguationData":[OSD([sQuery(id+"F0.wireOp",EDGE,"E75")])],"isStart":false});
            var Q5;
            Q5=makeQuery(id+"F16.opExtrude","CAP_EDGE",EDGE,{"disambiguationData":[OSD([sQuery(id+"F0.wireOp",EDGE,"E8")])],"isStart":false});
            var Q6;
            Q6=makeQuery(id+"F16.opExtrude","CAP_EDGE",EDGE,{"disambiguationData":[OSD([sQuery(id+"F0.wireOp",EDGE,"E9")])],"isStart":false});
            fillet(context, id + "F17", {"entities" : qUnion([Q0, Q1, Q2, Q3, Q4, Q5, Q6]), "radius" : 2 * mm, "tangentPropagation" : true, "allowEdgeOverflow" : false});
        }
    });
